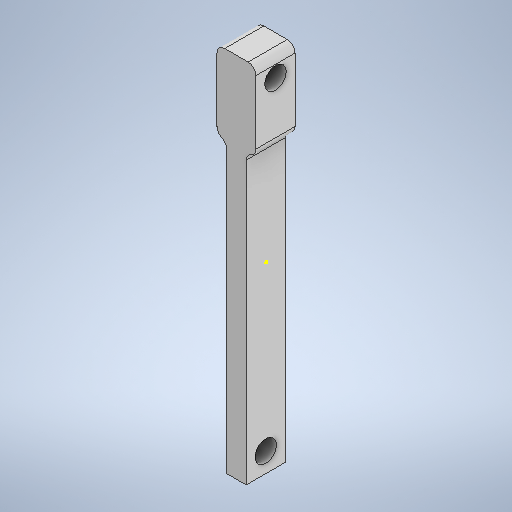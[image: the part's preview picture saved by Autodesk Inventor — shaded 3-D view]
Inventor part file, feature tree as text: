
AUTODESK INVENTOR PART (.ipt)
format: ipt  version: 2025.2 (Build 292293000, 293)  size: 279,040 bytes
history: native  units: mm
features: sketch x5, extrude x4, other x1, fillet x1
ambient origin geometry x8: Origin, YZ Plane, XZ Plane, XY Plane, X Axis, Y Axis, Z Axis, Center Point
bodies: Body1 (feature_tree)
feature tree (11):
  other  "Bryła1"
  extrude  "Wyciągnięcie proste1"  Depth=5.0mm
  extrude  "Wyciągnięcie proste3"  Depth=10.0mm
  sketch  "Szkic4"
  extrude  "Wyciągnięcie proste4"  Depth=94.0mm TaperAngle=0.0deg
  extrude  "Wyciągnięcie proste5"  Depth=5.5mm
  fillet  "Zaokrąglenie3"  Radius=5.0mm
  sketch  "Szkic1"
  sketch  "Szkic3"
  sketch  "Szkic5"
  sketch  "Szkic6"
